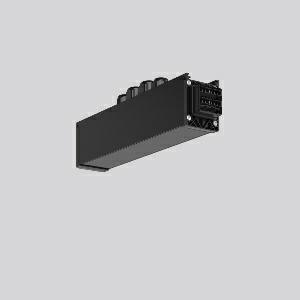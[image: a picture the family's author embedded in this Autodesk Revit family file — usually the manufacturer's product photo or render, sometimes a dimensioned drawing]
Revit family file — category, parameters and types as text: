
# Revit family: linedo_mitteleinspeisung_14pol_982698_003_710e
name_source: partatom
category: Lighting Fixtures
units: mm (PartAtom-declared; Revit-internal decimal feet)

## family parameters
Cut with Voids When Loaded = No
Host = Face
Light Source = No
Part Type = Normal
Room Calculation Point = No
Round Connector Dimension = Use Diameter
Shared = No

## types (1)
- LINEDO_Mitteleinspeisung_14pol
    Apparent Load = 0 VA
    Default Elevation = 1800 mm
    Description = Series: LINEDO
Middle power feed, 14-pole, connection socket / plug. Housing: extruded aluminium profile, powder-coated. Cover made of plastic, surface like housing. LINEDO plug system, plastic, black. 4 cable glands (2 x M20 and 2 x M25). Cable glands on top. Easy connection for rigid or flexible wires.
Colour: black
Length: 330 mm
Width: 58 mm
Height: 76 mm
Weight: 850 g
    Height = 76 mm
    Lamp = 0 x
    Length = 330 mm
    Luminous efficacy = 0 lm/W
    Manufacturer = RZB
    ModVariant = No
    Model = 982698.003
    Mounting Place = Ceiling
    Mounting Type = Pendant, Surface mounted
    Number of Poles = 1
    OnlyDefault = Yes
    Power Factor = 1
    Product Name = LINEDO_Mitteleinspeisung_14pol
    Product group = Surface mounted continuous line luminaire system
    ProductGroupID = 310
    Protection Class = Protection class I
    Protection Degree = IP 54
    RLX_Detail_Level = 1
    RLX_Emergency_Light_Flux = 0 lm
    RLX_Emergency_Type = 0
    RLX_Emergency_Type_DB = No
    RlxData = <blob elided: 23269 chars, md5=bbca4b8d>
    Standby Power = 0 W
    System Light Flux = 0 lm
    System Power = 0 W
    Type Comments = Product without accessories
    Type Image = 982698.003.jpg
    URL = http://relux.com
    VarID = ---
    Voltage = 0 V
    Weight = 0.00 kg
    Width = 58 mm

## geometry (parser evidence)
native form markers: Blend x4, Sweep x12
no freeform markers — native parametric forms only
